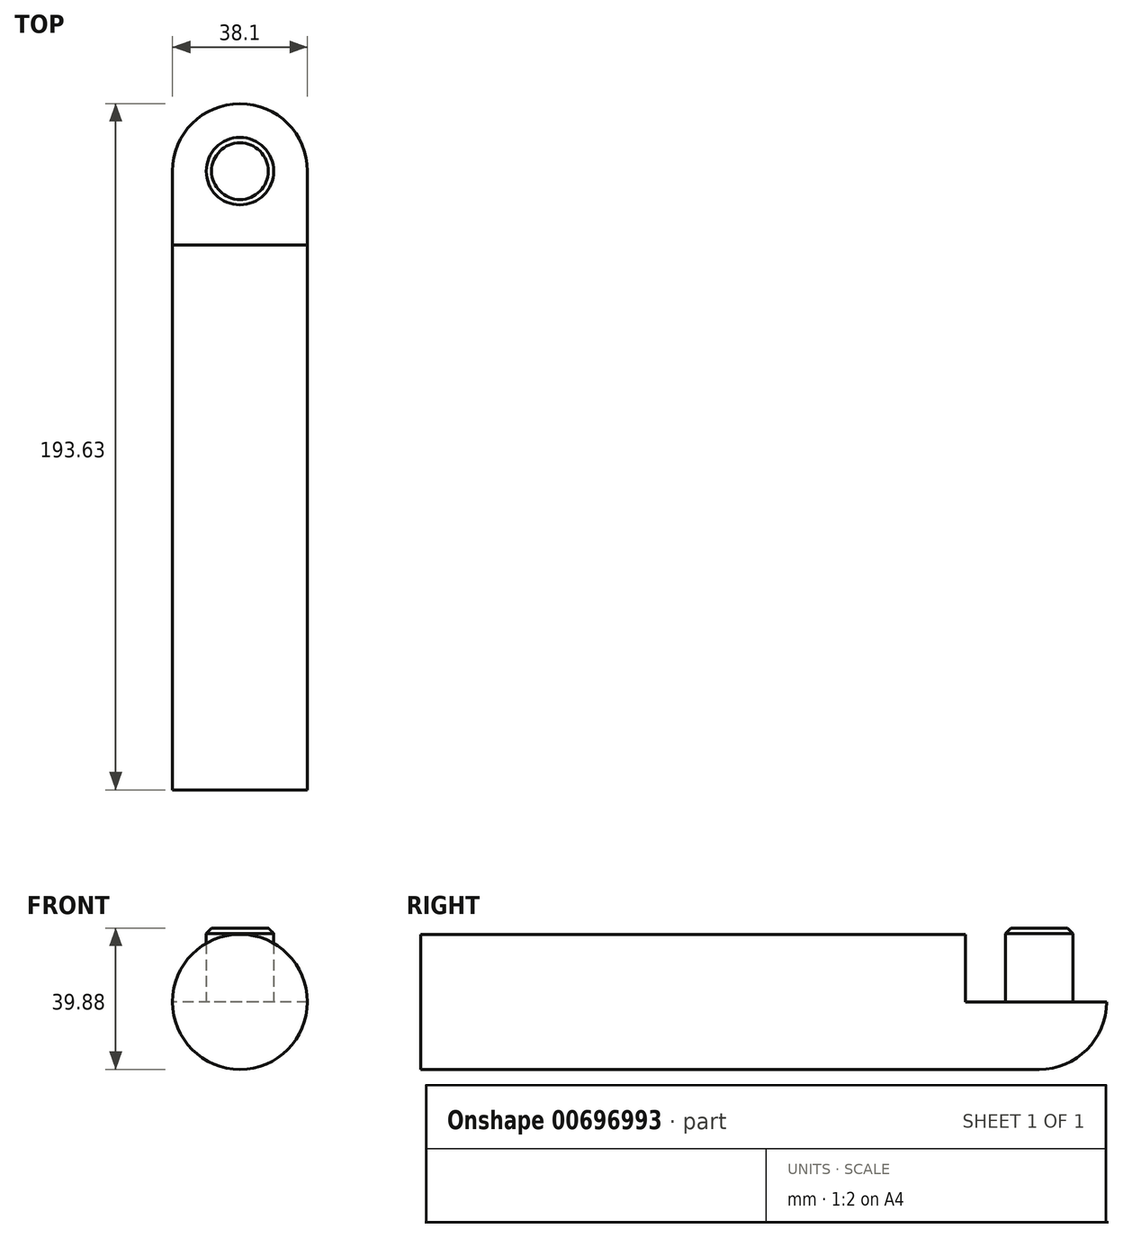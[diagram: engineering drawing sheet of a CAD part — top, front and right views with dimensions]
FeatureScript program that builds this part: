
annotation { "Feature Type Name" : "Feature", "Feature Type Description" : "" }
export const myFeature = defineFeature(function(context is Context, id is Id, definition is map)
    precondition{}
    {
        {
            var Q0;
            Q0=qCreatedBy(makeId("Front.planeOp"),FACE);
            var sketch = newSketch(context, id + "F0", { "sketchPlane" : qUnion([Q0])});
            skCircle(sketch, "E0", {"center": v(0, 0) * mm, "radius": 19.05 * mm});
            skSolve(sketch);
        }
        {
            var Q0;
            Q0=makeQuery(id+"F0.imprint","IMPRINT",FACE,{"disambiguationData":[TD([[makeQuery(id+"F0.imprint","IMPRINT",EDGE,{"derivedFrom":sQuery(id+"F0.wireOp",EDGE,"E0")}),1.0]])]});
            extrude(context, id + "F1", {"entities" : qUnion([Q0]), "depth" : 174.58 * mm});
        }
        {
            var Q0;
            Q0=makeQuery(id+"F1.opExtrude","CAP_FACE",FACE,{"disambiguationData":[OSD([sQuery(id+"F0.wireOp",EDGE,"E0")])],"isStart":true});
            var sketch = newSketch(context, id + "F2", { "sketchPlane" : qUnion([Q0])});
            skLineSegment(sketch, "E1", {"start": v(0, 0) * mm, "end": v(0, 21.19) * mm});
            skLineSegment(sketch, "E2", {"start": v(0, 21.19) * mm, "end": v(0, -25.37) * mm});
            skLineSegment(sketch, "E3", {"start": v(-20.84, 0) * mm, "end": v(39.79, 0) * mm});
            skSolve(sketch);
        }
        {
            var Q0;
            {var subQ0=sQuery(id+"F2.wireOp",EDGE,"E3");var subQ1=sQuery(id+"F2.wireOp",EDGE,"E2");var subQ2=makeQuery(id+"F2.imprint","INTERSECT",VERTEX,{"derivedFrom":[subQ1,subQ0]});Q0=makeQuery(id+"F2.imprint","IMPRINT",FACE,{"disambiguationData":[TD([[makeQuery(id+"F2.imprint","IMPRINT",EDGE,{"disambiguationData":[TD([[subQ2,-1.0]])],"derivedFrom":subQ1}),1.0]])]});}
            var Q1;
            Q1=sQuery(id+"F2.wireOp",EDGE,"E2");
            revolve(context, id + "F3", {"operationType" : NewBodyOperationType.ADD, "entities" : qUnion([Q0]), "axis" : qUnion([Q1]), "revolveType" : RevolveType.FULL});
        }
        {
            var Q0;
            Q0=makeQuery(id+"F1.opExtrude","CAP_FACE",FACE,{"disambiguationData":[OSD([sQuery(id+"F0.wireOp",EDGE,"E0")])],"isStart":true});
            extrude(context, id + "F4", {"entities" : qUnion([Q0]), "operationType" : NewBodyOperationType.REMOVE, "oppositeDirection" : true, "depth" : 20.83 * mm});
        }
        {
            var Q0;
            {var subQ0=sQuery(id+"F2.wireOp",EDGE,"E3");Q0=makeQuery(id+"F4.boolean.opBoolean","MERGE",FACE,{"derivedFrom":[makeQuery(id+"F3.opRevolve","SWEPT_FACE",FACE,{"disambiguationData":[OSD([subQ0])]}),makeQuery(id+"F4.opExtrude","SWEPT_FACE",FACE,{"disambiguationData":[OSD([sQuery(id+"F0.wireOp",EDGE,"E0"),subQ0])]})]});}
            var sketch = newSketch(context, id + "F5", { "sketchPlane" : qUnion([Q0])});
            skCircle(sketch, "E4", {"center": v(0, 0) * mm, "radius": 9.53 * mm});
            skSolve(sketch);
        }
        {
            var Q0;
            Q0=makeQuery(id+"F5.imprint","IMPRINT",FACE,{"disambiguationData":[TD([[makeQuery(id+"F5.imprint","IMPRINT",EDGE,{"derivedFrom":sQuery(id+"F5.wireOp",EDGE,"E4")}),1.0]])]});
            extrude(context, id + "F6", {"entities" : qUnion([Q0]), "operationType" : NewBodyOperationType.ADD, "depth" : 20.83 * mm});
        }
        {
            var Q0;
            Q0=makeQuery(id+"F6.opExtrude","CAP_EDGE",EDGE,{"disambiguationData":[OSD([sQuery(id+"F5.wireOp",EDGE,"E4")])],"isStart":false});
            chamfer(context, id + "F7", {"entities" : qUnion([Q0]), "chamferType" : ChamferType.OFFSET_ANGLE, "width" : 1.52 * mm, "oppositeDirection" : false, "angle" : 45 * degree, "tangentPropagation" : true});
        }
    });
